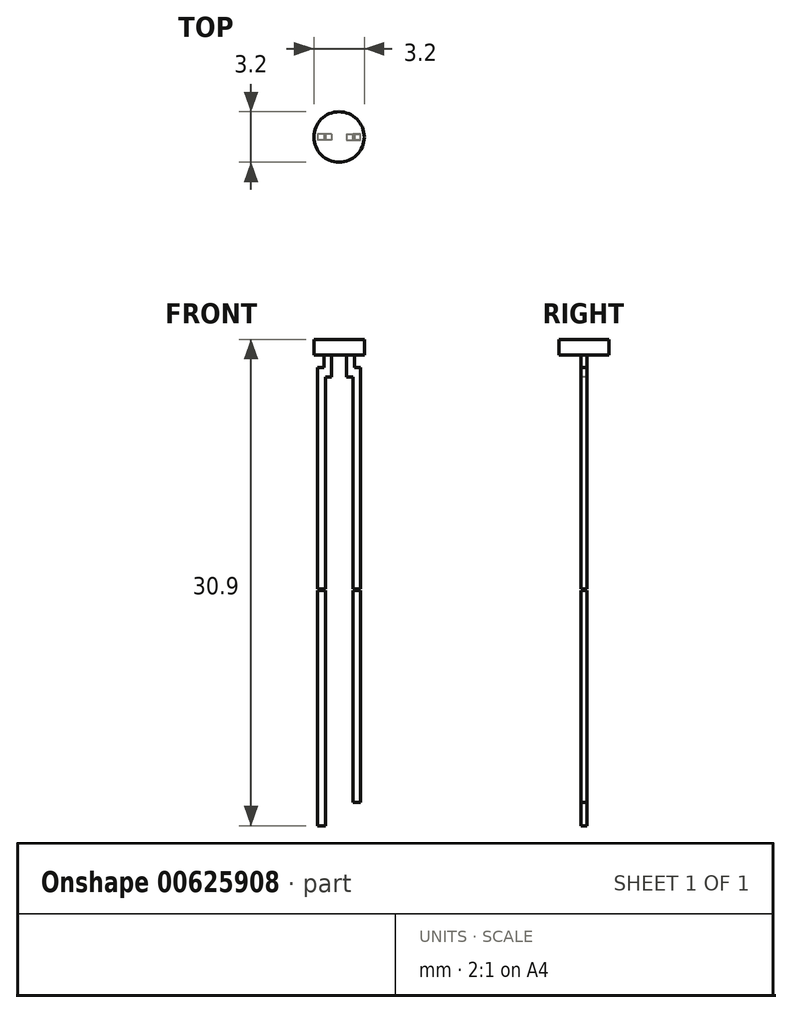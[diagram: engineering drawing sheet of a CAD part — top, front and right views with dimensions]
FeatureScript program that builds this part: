
annotation { "Feature Type Name" : "Feature", "Feature Type Description" : "" }
export const myFeature = defineFeature(function(context is Context, id is Id, definition is map)
    precondition{}
    {
        {
            var Q0;
            Q0=qCreatedBy(makeId("Front.planeOp"),FACE);
            var sketch = newSketch(context, id + "F0", { "sketchPlane" : qUnion([Q0])});
            skLineSegment(sketch, "E0.right", {"start": v(1.6, 1) * mm, "end": v(1.6, 0) * mm});
            skPoint(sketch, "E0.middle", {"position": v(0, 0) * mm});
            skLineSegment(sketch, "E1", {"start": v(0, 0) * mm, "end": v(0, 1) * mm});
            skLineSegment(sketch, "E2", {"start": v(0, 1) * mm, "end": v(1.6, 1) * mm});
            skLineSegment(sketch, "E3", {"start": v(0, 0) * mm, "end": v(1.6, 0) * mm});
            skPoint(sketch, "E4.endSnap0", {"position": v(0.8, 1) * mm});
            skLineSegment(sketch, "E5.bottom", {"start": v(0, 1) * mm, "end": v(1.45, 1) * mm});
            skLineSegment(sketch, "E5.top", {"start": v(0, 4.5) * mm, "end": v(0.05, 4.5) * mm});
            skLineSegment(sketch, "E5.left", {"start": v(0, 1) * mm, "end": v(0, 4.5) * mm});
            skLineSegment(sketch, "E5.right", {"start": v(1.45, 1) * mm, "end": v(1.45, 3.1) * mm});
            skPoint(sketch, "E6.visualSharp", {"position": v(1.45, 4.5) * mm});
            skArc(sketch, "E6.filletArc", {"start": v(1.45, 3.1) * mm, "mid": v(1.04, 4.09) * mm, "end": v(0.05, 4.5) * mm});
            skLineSegment(sketch, "E7", {"start": v(0, 0) * mm, "end": v(-0.47, 0) * mm});
            skLineSegment(sketch, "E8", {"start": v(-0.47, 0) * mm, "end": v(-0.47, -1.4) * mm});
            skLineSegment(sketch, "E9", {"start": v(-0.47, -1.4) * mm, "end": v(-0.87, -1.4) * mm});
            skLineSegment(sketch, "E10", {"start": v(-0.87, -1.4) * mm, "end": v(-0.87, -29.9) * mm});
            skLineSegment(sketch, "E11", {"start": v(-0.47, 0) * mm, "end": v(-0.97, 0) * mm});
            skLineSegment(sketch, "E12", {"start": v(-0.97, 0) * mm, "end": v(-0.97, -0.8) * mm});
            skLineSegment(sketch, "E13", {"start": v(-0.97, -0.8) * mm, "end": v(-1.37, -0.8) * mm});
            skLineSegment(sketch, "E14", {"start": v(-1.37, -0.8) * mm, "end": v(-1.37, -29.9) * mm});
            skLineSegment(sketch, "E15", {"start": v(-1.37, -29.9) * mm, "end": v(-0.87, -29.9) * mm});
            skLineSegment(sketch, "E16", {"start": v(0, 0) * mm, "end": v(0.47, 0) * mm});
            skLineSegment(sketch, "E17", {"start": v(0.47, 0) * mm, "end": v(0.47, -1.4) * mm});
            skLineSegment(sketch, "E18", {"start": v(0.47, -1.4) * mm, "end": v(0.87, -1.4) * mm});
            skLineSegment(sketch, "E19", {"start": v(0.87, -1.4) * mm, "end": v(0.87, -28.4) * mm});
            skLineSegment(sketch, "E20", {"start": v(0.87, -28.4) * mm, "end": v(1.37, -28.4) * mm});
            skLineSegment(sketch, "E21", {"start": v(0.47, 0) * mm, "end": v(0.97, 0) * mm});
            skLineSegment(sketch, "E22", {"start": v(0.97, 0) * mm, "end": v(0.97, -0.8) * mm});
            skLineSegment(sketch, "E23", {"start": v(0.97, -0.8) * mm, "end": v(1.37, -0.8) * mm});
            skLineSegment(sketch, "E24", {"start": v(1.37, -0.8) * mm, "end": v(1.37, -28.4) * mm});
            skLineSegment(sketch, "E25", {"start": v(-1.37, -14.97) * mm, "end": v(-0.87, -14.97) * mm});
            skPoint(sketch, "E25.endSnap0", {"position": v(-0.87, -15.65) * mm});
            skLineSegment(sketch, "E26", {"start": v(-0.87, -14.97) * mm, "end": v(-0.87, -14.87) * mm});
            skLineSegment(sketch, "E27", {"start": v(-0.87, -14.87) * mm, "end": v(-1.37, -14.87) * mm});
            skLineSegment(sketch, "E28", {"start": v(0.87, -14.87) * mm, "end": v(1.37, -14.87) * mm});
            skLineSegment(sketch, "E29", {"start": v(1.37, -14.87) * mm, "end": v(1.37, -14.97) * mm});
            skLineSegment(sketch, "E30", {"start": v(1.37, -14.97) * mm, "end": v(0.87, -14.97) * mm});
            skLineSegment(sketch, "E31", {"start": v(0.87, -14.97) * mm, "end": v(0.87, -14.87) * mm});
            skLineSegment(sketch, "E32", {"start": v(0.47, 0) * mm, "end": v(0.47, -0.65) * mm});
            skLineSegment(sketch, "E33", {"start": v(0.97, 0) * mm, "end": v(0.97, -0.65) * mm});
            skLineSegment(sketch, "E34", {"start": v(0.97, -0.65) * mm, "end": v(1.06, 0) * mm});
            skLineSegment(sketch, "E35", {"start": v(0.47, -0.65) * mm, "end": v(0.38, 0) * mm});
            skLineSegment(sketch, "E36", {"start": v(-0.47, 0) * mm, "end": v(-0.47, -0.65) * mm});
            skLineSegment(sketch, "E37", {"start": v(-0.47, -0.65) * mm, "end": v(-0.38, 0) * mm});
            skLineSegment(sketch, "E38", {"start": v(-0.97, 0) * mm, "end": v(-0.97, -0.65) * mm});
            skLineSegment(sketch, "E39", {"start": v(-0.97, -0.65) * mm, "end": v(-1.06, 0) * mm});
            skLineSegment(sketch, "E40", {"start": v(-1.06, 0) * mm, "end": v(-0.97, 0) * mm});
            skSolve(sketch);
        }
        {
            var Q0;
            Q0=makeQuery(id+"F0.imprint","IMPRINT",FACE,{"disambiguationData":[TD([[makeQuery(id+"F0.imprint","IMPRINT",EDGE,{"derivedFrom":sQuery(id+"F0.wireOp",EDGE,"E5.bottom")}),1.0]])]});
            var Q1;
            Q1=makeQuery(id+"F0.imprint","IMPRINT",FACE,{"disambiguationData":[TD([[makeQuery(id+"F0.imprint","IMPRINT",EDGE,{"derivedFrom":sQuery(id+"F0.wireOp",EDGE,"E0.right")}),-1.0]])]});
            var Q2;
            Q2=sQuery(id+"F0.wireOp",EDGE,"E5.left");
            revolve(context, id + "F1", {"entities" : qUnion([Q0, Q1]), "axis" : qUnion([Q2]), "revolveType" : RevolveType.FULL});
        }
        {
            var Q0;
            Q0=makeQuery(id+"F0.imprint","IMPRINT",FACE,{"disambiguationData":[TD([[makeQuery(id+"F0.imprint","IMPRINT",EDGE,{"derivedFrom":sQuery(id+"F0.wireOp",EDGE,"E17")}),1.0]])]});
            var Q1;
            Q1=makeQuery(id+"F0.imprint","IMPRINT",FACE,{"disambiguationData":[TD([[makeQuery(id+"F0.imprint","IMPRINT",EDGE,{"derivedFrom":sQuery(id+"F0.wireOp",EDGE,"E8")}),-1.0]])]});
            extrude(context, id + "F2", {"entities" : qUnion([Q0, Q1]), "operationType" : NewBodyOperationType.ADD, "endBound" : BoundingType.SYMMETRIC, "oppositeDirection" : true, "depth" : 0.4 * mm, "offsetDistance" : 25 * mm});
        }
        {
            var Q0;
            Q0=makeQuery(id+"F0.imprint","IMPRINT",FACE,{"disambiguationData":[TD([[makeQuery(id+"F0.imprint","IMPRINT",EDGE,{"derivedFrom":sQuery(id+"F0.wireOp",EDGE,"E28")}),-1.0]])]});
            var Q1;
            {var subQ0=sQuery(id+"F0.wireOp",EDGE,"E25");Q1=makeQuery(id+"F0.imprint","IMPRINT",FACE,{"disambiguationData":[TD([[makeQuery(id+"F0.imprint","IMPRINT",EDGE,{"derivedFrom":subQ0}),1.0]])]});}
            extrude(context, id + "F3", {"entities" : qUnion([Q0, Q1]), "operationType" : NewBodyOperationType.REMOVE, "endBound" : BoundingType.SYMMETRIC, "oppositeDirection" : true, "depth" : 0.4 * mm, "offsetDistance" : 25 * mm});
        }
        {
            var Q0;
            {var subQ0=sQuery(id+"F0.wireOp",EDGE,"E15");Q0=makeQuery(id+"F0.imprint","IMPRINT",FACE,{"disambiguationData":[TD([[makeQuery(id+"F0.imprint","IMPRINT",EDGE,{"derivedFrom":subQ0}),1.0]])]});}
            var Q1;
            {var subQ0=sQuery(id+"F0.wireOp",EDGE,"E20");Q1=makeQuery(id+"F0.imprint","IMPRINT",FACE,{"disambiguationData":[TD([[makeQuery(id+"F0.imprint","IMPRINT",EDGE,{"derivedFrom":subQ0}),1.0]])]});}
            extrude(context, id + "F4", {"entities" : qUnion([Q0, Q1]), "endBound" : BoundingType.SYMMETRIC, "depth" : 0.4 * mm, "offsetDistance" : 25 * mm});
        }
        {
            var Q0;
            Q0=sQuery(id+"F0.wireOp",EDGE,"E39");
            var Q1;
            Q1=sQuery(id+"F0.wireOp",EDGE,"E37");
            var Q2;
            Q2=sQuery(id+"F0.wireOp",EDGE,"E35");
            var Q3;
            Q3=sQuery(id+"F0.wireOp",EDGE,"E34");
            extrude(context, id + "F5", {"bodyType" : ToolBodyType.SURFACE, "surfaceEntities" : qUnion([Q0, Q1, Q2, Q3]), "endBound" : BoundingType.SYMMETRIC, "depth" : 0.4 * mm, "offsetDistance" : 25 * mm});
        }
    });
